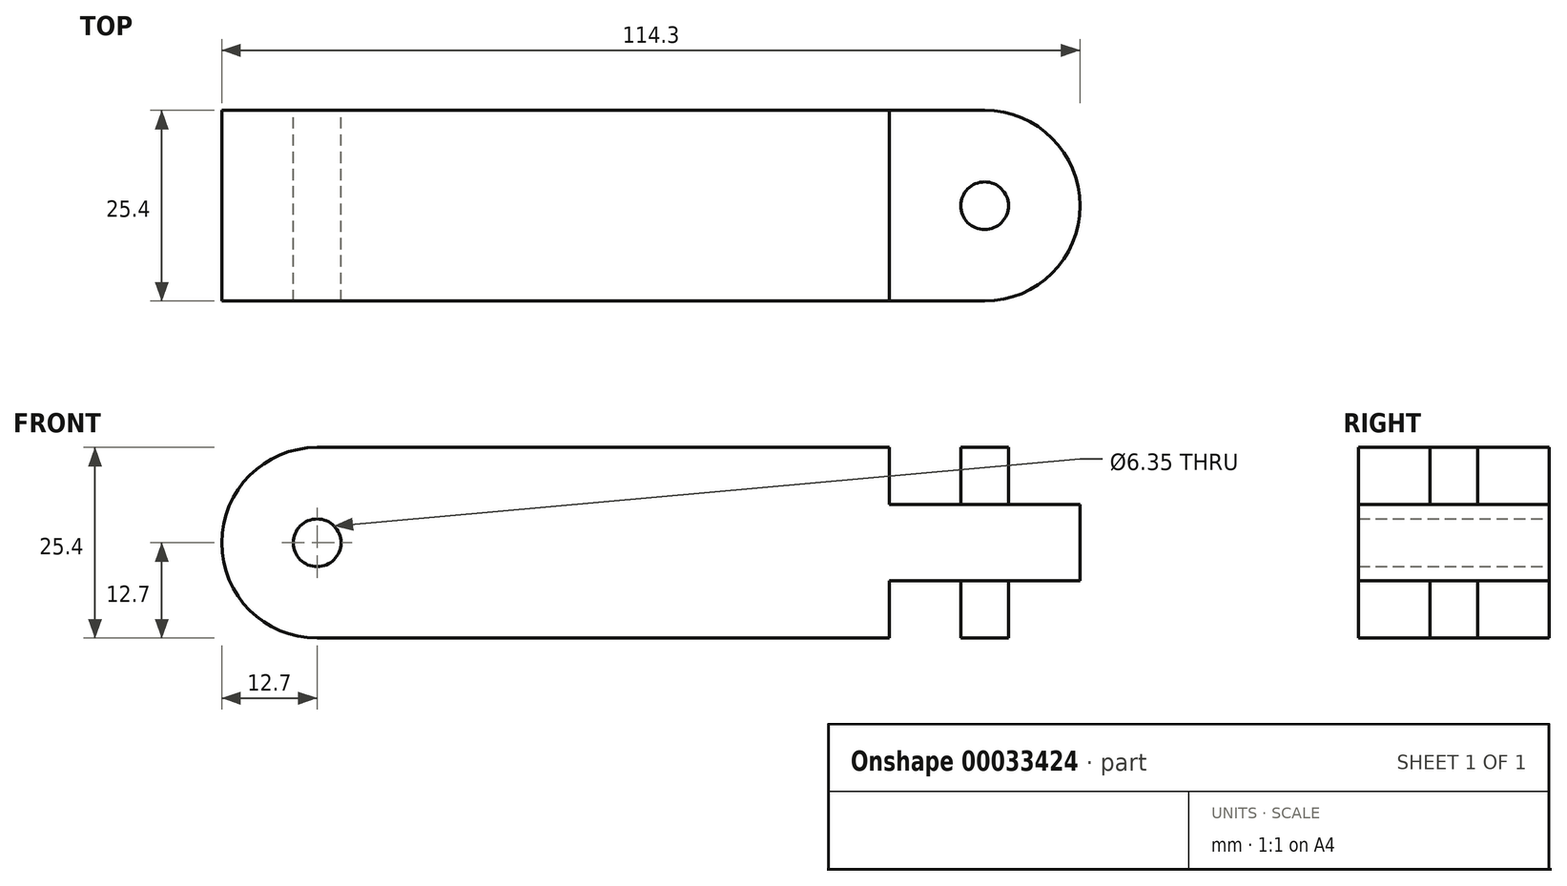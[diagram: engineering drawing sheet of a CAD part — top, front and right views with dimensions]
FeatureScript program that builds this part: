
annotation { "Feature Type Name" : "Feature", "Feature Type Description" : "" }
export const myFeature = defineFeature(function(context is Context, id is Id, definition is map)
    precondition{}
    {
        {
            var Q0;
            Q0=qCreatedBy(makeId("Front.planeOp"),FACE);
            var sketch = newSketch(context, id + "F0", { "sketchPlane" : qUnion([Q0])});
            skLineSegment(sketch, "E0.rect.bottom", {"start": v(-38.1, 12.7) * mm, "end": v(38.1, 12.7) * mm});
            skLineSegment(sketch, "E0.rect.top", {"start": v(-38.1, -12.7) * mm, "end": v(38.1, -12.7) * mm});
            skLineSegment(sketch, "E0.rect.right", {"start": v(38.1, 12.7) * mm, "end": v(38.1, -12.7) * mm});
            skPoint(sketch, "E0.rect.middle", {"position": v(0, 0) * mm});
            skArc(sketch, "E1", {"start": v(-38.1, 12.7) * mm, "mid": v(-50.8, 0) * mm, "end": v(-38.1, -12.7) * mm});
            skCircle(sketch, "E2", {"center": v(-38.1, 0) * mm, "radius": 3.18 * mm});
            skSolve(sketch);
        }
        {
            var Q0;
            Q0 = qSketchRegion(id + "F0", true);
            extrude(context, id + "F1", {"entities" : qUnion([Q0]), "depth" : 25.4 * mm});
        }
        {
            var Q0;
            Q0=makeQuery(id+"F1.opExtrude","SWEPT_FACE",FACE,{"disambiguationData":[OSD([sQuery(id+"F0.wireOp",EDGE,"E0.rect.right")])]});
            var sketch = newSketch(context, id + "F2", { "sketchPlane" : qUnion([Q0])});
            skPoint(sketch, "E3", {"position": v(-25.4, 0) * mm});
            skPoint(sketch, "E4", {"position": v(0, 0) * mm});
            skLineSegment(sketch, "E5.bottom", {"start": v(-25.4, 5.08) * mm, "end": v(0, 5.08) * mm});
            skLineSegment(sketch, "E5.top", {"start": v(-25.4, -5.08) * mm, "end": v(0, -5.08) * mm});
            skLineSegment(sketch, "E5.left", {"start": v(-25.4, 5.08) * mm, "end": v(-25.4, -5.08) * mm});
            skLineSegment(sketch, "E5.right", {"start": v(0, 5.08) * mm, "end": v(0, -5.08) * mm});
            skSolve(sketch);
        }
        {
            var Q0;
            Q0 = qSketchRegion(id + "F2", true);
            extrude(context, id + "F3", {"entities" : qUnion([Q0]), "operationType" : NewBodyOperationType.ADD, "depth" : 25.4 * mm});
        }
        {
            var Q0;
            Q0=makeQuery(id+"F3.opExtrude","SWEPT_FACE",FACE,{"disambiguationData":[OSD([sQuery(id+"F2.wireOp",EDGE,"E5.bottom")])]});
            var sketch = newSketch(context, id + "F4", { "sketchPlane" : qUnion([Q0])});
            skCircle(sketch, "E6", {"center": v(50.8, -12.7) * mm, "radius": 12.7 * mm});
            skPoint(sketch, "E6.first.point", {"position": v(50.8, 0) * mm});
            skPoint(sketch, "E6.second.point", {"position": v(63.5, -12.7) * mm});
            skPoint(sketch, "E6.third.point", {"position": v(38.1, -12.7) * mm});
            skCircle(sketch, "E7", {"center": v(50.8, -12.7) * mm, "radius": 3.18 * mm});
            skSolve(sketch);
        }
        {
            var Q0;
            {var subQ0=sQuery(id+"F2.wireOp",EDGE,"E5.bottom");var subQ1=makeQuery(id+"F3.opExtrude","CAP_EDGE",EDGE,{"disambiguationData":[OSD([subQ0])],"isStart":false});var subQ2=sQuery(id+"F4.wireOp",EDGE,"E6");var subQ3=makeQuery(id+"F4.imprint","INTERSECT",VERTEX,{"derivedFrom":[subQ1,subQ2]});Q0=makeQuery(id+"F4.imprint","IMPRINT",FACE,{"disambiguationData":[TD([[makeQuery(id+"F4.imprint","IMPRINT",EDGE,{"disambiguationData":[TD([[subQ3,-1.0]])],"derivedFrom":subQ2}),-1.0]])]});}
            var Q1;
            {var subQ0=sQuery(id+"F2.wireOp",EDGE,"E5.bottom");var subQ1=makeQuery(id+"F3.opExtrude","CAP_EDGE",EDGE,{"disambiguationData":[OSD([subQ0])],"isStart":false});var subQ2=sQuery(id+"F4.wireOp",EDGE,"E6");var subQ3=makeQuery(id+"F4.imprint","INTERSECT",VERTEX,{"derivedFrom":[subQ1,subQ2]});Q1=makeQuery(id+"F4.imprint","IMPRINT",FACE,{"disambiguationData":[TD([[makeQuery(id+"F4.imprint","IMPRINT",EDGE,{"disambiguationData":[TD([[subQ3,1.0]])],"derivedFrom":subQ2}),-1.0]])]});}
            extrude(context, id + "F5", {"entities" : qUnion([Q0, Q1]), "operationType" : NewBodyOperationType.REMOVE, "oppositeDirection" : true, "depth" : 25.4 * mm});
        }
        {
            var Q0;
            Q0=makeQuery(id+"F4.imprint","IMPRINT",FACE,{"disambiguationData":[TD([[makeQuery(id+"F4.imprint","IMPRINT",EDGE,{"derivedFrom":sQuery(id+"F4.wireOp",EDGE,"E7")}),1.0]])]});
            var Q1;
            Q1=sQuery(id+"F4.wireOp",EDGE,"E7");
            extrude(context, id + "F6", {"entities" : qUnion([Q0]), "operationType" : NewBodyOperationType.ADD, "surfaceEntities" : qUnion([Q1]), "depth" : 7.62 * mm});
        }
        {
            var Q0;
            Q0=makeQuery(id+"F6.opExtrude","CAP_FACE",FACE,{"disambiguationData":[OSD([sQuery(id+"F4.wireOp",EDGE,"E7")])],"isStart":false});
            extrude(context, id + "F7", {"entities" : qUnion([Q0]), "operationType" : NewBodyOperationType.ADD, "oppositeDirection" : true, "depth" : 25.4 * mm});
        }
    });
